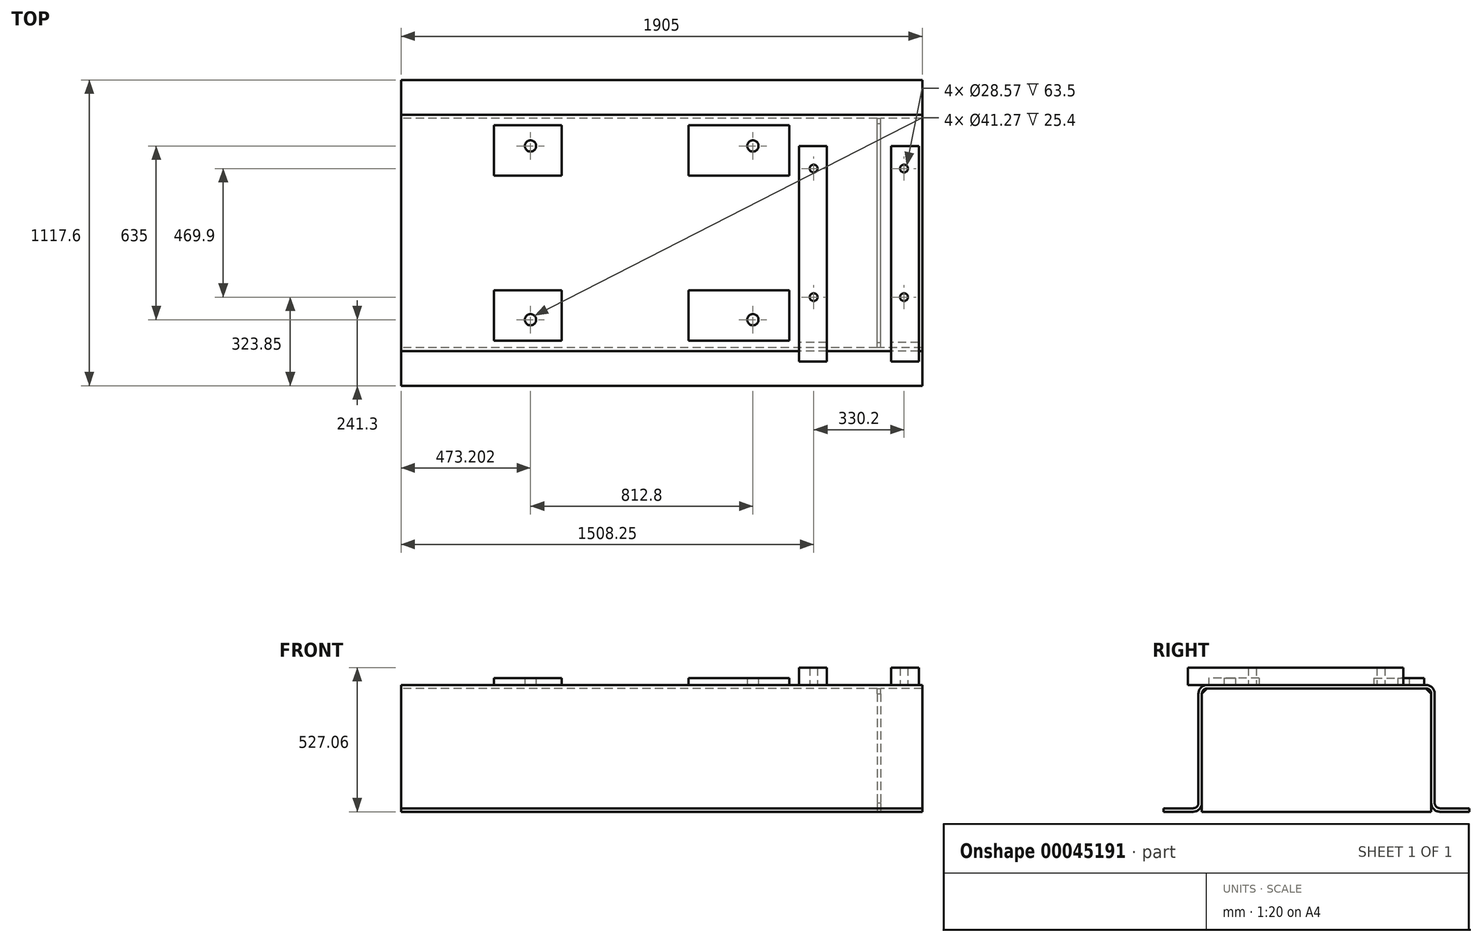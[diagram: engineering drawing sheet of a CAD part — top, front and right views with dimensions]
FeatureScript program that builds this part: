
annotation { "Feature Type Name" : "Feature", "Feature Type Description" : "" }
export const myFeature = defineFeature(function(context is Context, id is Id, definition is map)
    precondition{}
    {
        {
            var Q0;
            Q0=qCreatedBy(makeId("Right.planeOp"),FACE);
            var sketch = newSketch(context, id + "F0", { "sketchPlane" : qUnion([Q0])});
            skLineSegment(sketch, "E0.rect.bottom", {"start": v(-400.05, 231.78) * mm, "end": v(400.05, 231.78) * mm});
            skLineSegment(sketch, "E0.rect.top", {"start": v(-558.8, -231.78) * mm, "end": v(-450.85, -231.78) * mm});
            skLineSegment(sketch, "E0.rect.left", {"start": v(-431.8, 200.03) * mm, "end": v(-431.8, -200.03) * mm});
            skLineSegment(sketch, "E0.rect.right", {"start": v(431.8, 200.03) * mm, "end": v(431.8, -200.03) * mm});
            skPoint(sketch, "E0.rect.middle", {"position": v(0, 0) * mm});
            skLineSegment(sketch, "E1.0", {"start": v(-400.05, 219.08) * mm, "end": v(400.05, 219.08) * mm});
            skLineSegment(sketch, "E1.1", {"start": v(-419.1, 200.03) * mm, "end": v(-419.1, -200.03) * mm});
            skLineSegment(sketch, "E1.2", {"start": v(-558.8, -219.08) * mm, "end": v(-450.85, -219.08) * mm});
            skLineSegment(sketch, "E1.3", {"start": v(419.1, 200.03) * mm, "end": v(419.1, -200.03) * mm});
            skLineSegment(sketch, "E2.0", {"start": v(-558.8, -219.08) * mm, "end": v(-558.8, -231.78) * mm});
            skLineSegment(sketch, "E3", {"start": v(0, 0) * mm, "end": v(0, 438.25) * mm, "construction": true});
            skPoint(sketch, "E4.orphan", {"position": v(-431.8, -231.78) * mm});
            skLineSegment(sketch, "E5.MirrorCS", {"start": v(558.8, -219.08) * mm, "end": v(558.8, -231.78) * mm});
            skLineSegment(sketch, "E6.MirrorCS", {"start": v(558.8, -219.08) * mm, "end": v(450.85, -219.08) * mm});
            skLineSegment(sketch, "E7.MirrorCS", {"start": v(558.8, -231.78) * mm, "end": v(450.85, -231.78) * mm});
            skPoint(sketch, "E8.MirrorP", {"position": v(431.8, -231.78) * mm});
            skPoint(sketch, "E9.visualSharp", {"position": v(-431.8, -219.08) * mm});
            skArc(sketch, "E9.filletArc", {"start": v(-450.85, -219.08) * mm, "mid": v(-437.38, -213.5) * mm, "end": v(-431.8, -200.03) * mm});
            skPoint(sketch, "E10.visualSharp", {"position": v(-419.1, 219.08) * mm});
            skArc(sketch, "E10.filletArc", {"start": v(-400.05, 219.08) * mm, "mid": v(-413.52, 213.5) * mm, "end": v(-419.1, 200.03) * mm});
            skPoint(sketch, "E11.visualSharp", {"position": v(419.1, 219.08) * mm});
            skArc(sketch, "E11.filletArc", {"start": v(419.1, 200.03) * mm, "mid": v(413.52, 213.5) * mm, "end": v(400.05, 219.08) * mm});
            skPoint(sketch, "E12.visualSharp", {"position": v(431.8, -219.08) * mm});
            skArc(sketch, "E12.filletArc", {"start": v(431.8, -200.03) * mm, "mid": v(437.38, -213.5) * mm, "end": v(450.85, -219.08) * mm});
            skPoint(sketch, "E13.visualSharp", {"position": v(-419.1, -231.78) * mm});
            skArc(sketch, "E13.filletArc", {"start": v(-450.85, -231.78) * mm, "mid": v(-428.4, -222.48) * mm, "end": v(-419.1, -200.03) * mm});
            skPoint(sketch, "E14.visualSharp", {"position": v(-431.8, 231.78) * mm});
            skArc(sketch, "E14.filletArc", {"start": v(-400.05, 231.78) * mm, "mid": v(-422.5, 222.48) * mm, "end": v(-431.8, 200.03) * mm});
            skPoint(sketch, "E15.visualSharp", {"position": v(431.8, 231.78) * mm});
            skArc(sketch, "E15.filletArc", {"start": v(431.8, 200.03) * mm, "mid": v(422.5, 222.48) * mm, "end": v(400.05, 231.78) * mm});
            skPoint(sketch, "E16.visualSharp", {"position": v(419.1, -231.78) * mm});
            skArc(sketch, "E16.filletArc", {"start": v(419.1, -200.03) * mm, "mid": v(428.4, -222.48) * mm, "end": v(450.85, -231.78) * mm});
            skSolve(sketch);
        }
        {
            var Q0;
            Q0 = qSketchRegion(id + "F0", true);
            extrude(context, id + "F1", {"entities" : qUnion([Q0]), "endBound" : BoundingType.SYMMETRIC, "depth" : 1905 * mm});
        }
        {
            var Q0;
            Q0=makeQuery(id+"F1.opExtrude","SWEPT_FACE",FACE,{"disambiguationData":[OSD([sQuery(id+"F0.wireOp",EDGE,"E0.rect.bottom")])]});
            var sketch = newSketch(context, id + "F2", { "sketchPlane" : qUnion([Q0])});
            skLineSegment(sketch, "E17", {"start": v(-1090.5, 0) * mm, "end": v(1245.35, 0) * mm, "construction": true});
            skLineSegment(sketch, "E18.0", {"start": v(-952.5, -400.05) * mm, "end": v(-952.5, 400.05) * mm, "construction": true});
            skLineSegment(sketch, "E19.0", {"start": v(-72.9, -400.05) * mm, "end": v(-72.9, 400.05) * mm, "construction": true});
            skLineSegment(sketch, "E20.0", {"start": v(720.85, -400.05) * mm, "end": v(720.85, 400.05) * mm, "construction": true});
            skLineSegment(sketch, "E21.0", {"start": v(838.2, -469.9) * mm, "end": v(838.2, 317.5) * mm});
            skLineSegment(sketch, "E22.0", {"start": v(939.8, -469.9) * mm, "end": v(939.8, 317.5) * mm});
            skLineSegment(sketch, "E23.0", {"start": v(-1090.5, 317.5) * mm, "end": v(-72.9, 317.5) * mm});
            skLineSegment(sketch, "E24.0", {"start": v(838.2, -469.9) * mm, "end": v(939.8, -469.9) * mm});
            skLineSegment(sketch, "E25.trimOffspring", {"start": v(838.2, 317.5) * mm, "end": v(939.8, 317.5) * mm});
            skLineSegment(sketch, "E26.0", {"start": v(885.95, -400.05) * mm, "end": v(885.95, 400.05) * mm, "construction": true});
            skLineSegment(sketch, "E27.0", {"start": v(-1090.5, 234.95) * mm, "end": v(1245.35, 234.95) * mm, "construction": true});
            skLineSegment(sketch, "E28.0", {"start": v(-1090.5, -234.95) * mm, "end": v(1245.35, -234.95) * mm, "construction": true});
            skCircle(sketch, "E29", {"center": v(885.95, 234.95) * mm, "radius": 14.29 * mm});
            skCircle(sketch, "E30.MirrorC", {"center": v(885.95, -234.95) * mm, "radius": 14.29 * mm});
            skCircle(sketch, "E31.MirrorC", {"center": v(555.75, -234.95) * mm, "radius": 14.29 * mm});
            skCircle(sketch, "E32.MirrorC", {"center": v(555.75, 234.95) * mm, "radius": 14.29 * mm});
            skLineSegment(sketch, "E33.MirrorCS", {"start": v(603.5, -469.9) * mm, "end": v(501.9, -469.9) * mm});
            skLineSegment(sketch, "E34.MirrorCS", {"start": v(603.5, 317.5) * mm, "end": v(501.9, 317.5) * mm});
            skLineSegment(sketch, "E35.MirrorCS", {"start": v(603.5, -469.9) * mm, "end": v(603.5, 317.5) * mm});
            skLineSegment(sketch, "E36.MirrorCS", {"start": v(501.9, -469.9) * mm, "end": v(501.9, 317.5) * mm});
            skSolve(sketch);
        }
        {
            var Q0;
            Q0 = qSketchRegion(id + "F2", true);
            extrude(context, id + "F3", {"entities" : qUnion([Q0]), "operationType" : NewBodyOperationType.ADD, "depth" : 63.5 * mm});
        }
        {
            var Q0;
            {var subQ6=sQuery(id+"F2.wireOp",EDGE,"E25.trimOffspring");Q0=makeQuery(id+"F2.imprint","IMPRINT",FACE,{"disambiguationData":[TD([[makeQuery(id+"F2.imprint","IMPRINT",EDGE,{"derivedFrom":subQ6}),1.0]])]});}
            var sketch = newSketch(context, id + "F4", { "sketchPlane" : qUnion([Q0])});
            skLineSegment(sketch, "E37.0", {"start": v(98.55, -400.05) * mm, "end": v(98.55, 400.05) * mm, "construction": true});
            skLineSegment(sketch, "E38.0", {"start": v(466.85, -400.05) * mm, "end": v(466.85, 400.05) * mm, "construction": true});
            skLineSegment(sketch, "E39.0", {"start": v(-365, -400.05) * mm, "end": v(-365, 400.05) * mm, "construction": true});
            skLineSegment(sketch, "E40.0", {"start": v(-612.65, -400.05) * mm, "end": v(-612.65, 400.05) * mm, "construction": true});
            skLineSegment(sketch, "E41.0", {"start": v(-1090.5, -209.55) * mm, "end": v(1245.35, -209.55) * mm, "construction": true});
            skLineSegment(sketch, "E42.0", {"start": v(-1090.5, -393.7) * mm, "end": v(1245.35, -393.7) * mm, "construction": true});
            skLineSegment(sketch, "E43.bottom", {"start": v(466.85, -209.55) * mm, "end": v(98.55, -209.55) * mm});
            skLineSegment(sketch, "E43.top", {"start": v(466.85, -393.7) * mm, "end": v(98.55, -393.7) * mm});
            skLineSegment(sketch, "E43.left", {"start": v(466.85, -209.55) * mm, "end": v(466.85, -393.7) * mm});
            skLineSegment(sketch, "E43.right", {"start": v(98.55, -209.55) * mm, "end": v(98.55, -393.7) * mm});
            skLineSegment(sketch, "E44.bottom", {"start": v(-365, -209.55) * mm, "end": v(-612.65, -209.55) * mm});
            skLineSegment(sketch, "E44.top", {"start": v(-365, -393.7) * mm, "end": v(-612.65, -393.7) * mm});
            skLineSegment(sketch, "E44.left", {"start": v(-365, -209.55) * mm, "end": v(-365, -393.7) * mm});
            skLineSegment(sketch, "E44.right", {"start": v(-612.65, -209.55) * mm, "end": v(-612.65, -393.7) * mm});
            skLineSegment(sketch, "E45.0", {"start": v(333.5, -400.05) * mm, "end": v(333.5, 400.05) * mm, "construction": true});
            skLineSegment(sketch, "E46.0", {"start": v(-479.3, -400.05) * mm, "end": v(-479.3, 400.05) * mm, "construction": true});
            skLineSegment(sketch, "E47.0", {"start": v(-1090.5, -317.5) * mm, "end": v(1245.35, -317.5) * mm, "construction": true});
            skCircle(sketch, "E48", {"center": v(-479.3, -317.5) * mm, "radius": 20.64 * mm});
            skCircle(sketch, "E49", {"center": v(333.5, -317.5) * mm, "radius": 20.64 * mm});
            skCircle(sketch, "E50.MirrorC", {"center": v(333.5, 317.5) * mm, "radius": 20.64 * mm});
            skCircle(sketch, "E51.MirrorC", {"center": v(-479.3, 317.5) * mm, "radius": 20.64 * mm});
            skLineSegment(sketch, "E52.MirrorCS", {"start": v(-612.65, 209.55) * mm, "end": v(-612.65, 393.7) * mm});
            skLineSegment(sketch, "E53.MirrorCS", {"start": v(-365, 209.55) * mm, "end": v(-365, 393.7) * mm});
            skLineSegment(sketch, "E54.MirrorCS", {"start": v(-365, 393.7) * mm, "end": v(-612.65, 393.7) * mm});
            skLineSegment(sketch, "E55.MirrorCS", {"start": v(466.85, 209.55) * mm, "end": v(98.55, 209.55) * mm});
            skLineSegment(sketch, "E56.MirrorCS", {"start": v(466.85, 393.7) * mm, "end": v(98.55, 393.7) * mm});
            skLineSegment(sketch, "E57.MirrorCS", {"start": v(466.85, 209.55) * mm, "end": v(466.85, 393.7) * mm});
            skLineSegment(sketch, "E58.MirrorCS", {"start": v(98.55, 209.55) * mm, "end": v(98.55, 393.7) * mm});
            skLineSegment(sketch, "E59.MirrorCS", {"start": v(-365, 209.55) * mm, "end": v(-612.65, 209.55) * mm});
            skSolve(sketch);
        }
        {
            var Q0;
            Q0 = qSketchRegion(id + "F4", true);
            extrude(context, id + "F5", {"entities" : qUnion([Q0]), "operationType" : NewBodyOperationType.ADD, "depth" : 25.4 * mm});
        }
        {
            var Q0;
            Q0=makeQuery(id+"F1.opExtrude","CAP_FACE",FACE,{"disambiguationData":[OSD([sQuery(id+"F0.wireOp",EDGE,"E0.rect.bottom"),sQuery(id+"F0.wireOp",EDGE,"E0.rect.top"),sQuery(id+"F0.wireOp",EDGE,"E0.rect.left"),sQuery(id+"F0.wireOp",EDGE,"E0.rect.right"),sQuery(id+"F0.wireOp",EDGE,"E1.0"),sQuery(id+"F0.wireOp",EDGE,"E1.1"),sQuery(id+"F0.wireOp",EDGE,"E1.2"),sQuery(id+"F0.wireOp",EDGE,"E1.3"),sQuery(id+"F0.wireOp",EDGE,"E2.0"),sQuery(id+"F0.wireOp",EDGE,"E5.MirrorCS"),sQuery(id+"F0.wireOp",EDGE,"E6.MirrorCS"),sQuery(id+"F0.wireOp",EDGE,"E7.MirrorCS"),sQuery(id+"F0.wireOp",EDGE,"E9.filletArc"),sQuery(id+"F0.wireOp",EDGE,"E10.filletArc"),sQuery(id+"F0.wireOp",EDGE,"E11.filletArc"),sQuery(id+"F0.wireOp",EDGE,"E12.filletArc"),sQuery(id+"F0.wireOp",EDGE,"E13.filletArc"),sQuery(id+"F0.wireOp",EDGE,"E14.filletArc"),sQuery(id+"F0.wireOp",EDGE,"E15.filletArc"),sQuery(id+"F0.wireOp",EDGE,"E16.filletArc")])],"isStart":false});
            cPlane(context, id + "F6", {"entities" : qUnion([Q0]), "cplaneType" : CPlaneType.OFFSET, "offset" : 152.4 * mm, "oppositeDirection" : true, "width" : 152.4 * mm, "height" : 152.4 * mm});
        }
        {
            var Q0;
            Q0=qCreatedBy(id+"F6.planeOp",FACE);
            var sketch = newSketch(context, id + "F7", { "sketchPlane" : qUnion([Q0])});
            skLineSegment(sketch, "E60.0", {"start": v(-400.05, 219.08) * mm, "end": v(400.05, 219.08) * mm});
            skLineSegment(sketch, "E61.0", {"start": v(-419.1, 200.03) * mm, "end": v(-419.1, -231.78) * mm});
            skLineSegment(sketch, "E62.0", {"start": v(419.1, 200.03) * mm, "end": v(419.1, -231.78) * mm});
            skLineSegment(sketch, "E63.0", {"start": v(-558.8, -231.78) * mm, "end": v(419.1, -231.78) * mm});
            skLineSegment(sketch, "E64", {"start": v(-419.1, 200.03) * mm, "end": v(-400.05, 219.08) * mm});
            skLineSegment(sketch, "E65", {"start": v(400.05, 219.08) * mm, "end": v(419.1, 200.03) * mm});
            skPoint(sketch, "E66.orphan", {"position": v(-450.85, -231.78) * mm});
            skPoint(sketch, "E67.orphan", {"position": v(419.1, -200.03) * mm});
            skPoint(sketch, "E68.orphan", {"position": v(-419.1, -200.03) * mm});
            skSolve(sketch);
        }
        {
            var Q0;
            Q0 = qSketchRegion(id + "F7", true);
            extrude(context, id + "F8", {"entities" : qUnion([Q0]), "operationType" : NewBodyOperationType.ADD, "oppositeDirection" : true, "depth" : 12.7 * mm});
        }
    });
